# Revit family: Power-ModularDevices-GEWISS-90RCD-BDHP_2P
name_source: partatom
category: Apparecchi elettrici
revit_build: Autodesk Revit MEP 2016 (Build: 20150220_1215(x64)
units: mm (PartAtom-declared; Revit-internal decimal feet)

## family parameters
Condiviso = Sì
Host = Superficie
Mantenere orientamento annotazione = Sì
Numero OmniClass = 23.80.50.00
Punto di calcolo locali = Sì
Quota connettore circolare = Usa diametro
Taglio con vuoti quando caricato = No
Tipo di parte = Normale
Titolo OmniClass = Terminals for Power Supply

## types (1)
- Power-ModularDevices-GEWISS-90RCD-BDHP_2P
    Assembly position: = Any
    Catalogue = POWER
    Catalogue Range = 90 RCD
    Description = HIGH PERFORMANCE  RESIDUAL CURRENT DEVICE
    Descrizione = HP ADD-ON RCD 2P In<125A SEL.A/1 4M
    EAN code = 8011564116627
    Electrocod = 1412
    IDF = 111c2b23-8161-45d7-9b90-cf89a61cff0e
    IDT = cb6c7a3d-76c8-4146-b43f-86488f3e6643
    Idn = 1000MA
    Immagine tipo = GW95470.jpg
    Insulation voltage = 500V
    Label = BDHP
    Level of immunity (8/20 µs) = 3000A
    Modello = GW95470
    No. Chorus modules = 4
    No. modules = 4
    No. of modules EN 50022 = 4
    No. of poles = 2P
    Number of poles = 2P
    Numero di poli_ = 1
    Operating temperature = -25 +40 °C
    Overvoltage category = III
    Produttore = GEWISS S.p.A.
    Prospetto di default = 1219 mm
    Rated current (In) = 125A
    Rated current: = 125A
    Rated frequency (Hz) = 50/60 Hz
    Rated impulse withstand voltage = 4KV
    Rated insulation voltage (Ui) = 500V
    Rated residual operating current = 1000 mA
    Rated tightening torque = 3.5 / 3 (terminals)
    Rated voltage = 230V
    Rated voltage (IEC/EN 61009-1 app. G, IEC/EN 61009-2-1 app. G) = 230V
    SEO = Add-on RCD
    Section flexible cable = Max 50 mm²
    Section rigid cable = Max 70 mm²
    Spostamento_x = -340 mm
    Standard = EN61009-1 dev. G
    Standard; = IEC/EN 61009-1 app. G, IEC/EN 61009-2-1 app. G
    Stocking temperature = -40 +70 °C
    Technical sheet = https://www.gewiss.com
    Type = A(S)
    Type: = A[S]
    URL = https://www.gewiss.com
    Version file RFA = 19.0
    carico = Altro
    potenza in watt = 0 V
